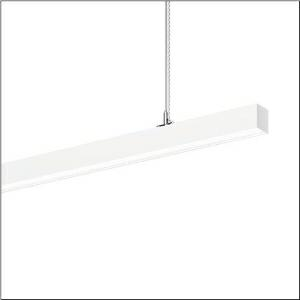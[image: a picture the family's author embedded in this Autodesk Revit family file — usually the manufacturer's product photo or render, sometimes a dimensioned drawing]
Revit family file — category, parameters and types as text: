
# Revit family: silica_r__21_51mx33da47wb_07b3
name_source: partatom
category: Lighting Fixtures
units: mm (PartAtom-declared; Revit-internal decimal feet)

## family parameters
Cut with Voids When Loaded = No
Host = Face
Light Source = No
Part Type = Normal
Room Calculation Point = No
Round Connector Dimension = Use Diameter
Shared = No

## types (1)
- --- (1 x LED, 5910 lm, 38.4 W, 4000K)
    Apparent Load = 38 VA
    CIE Flux Codes = 78 96 99 55 100
    Color Rendering = 80
    Color Temperature = 4000K
    Default Elevation = 1800 mm
    Description = Silica® 21, office luminaire, primary optical cover: prismatic diffuser, of PMMA, CAT 2 (L<= 3000cd/m²), light emission: direct/indirect distribution, primary light characteristic: symmetric, installation type: suspended mounting, LED, rated luminous flux: 5.910lm, luminous efficacy: 154lm/W, light colour: 840, colour temperature: 4000K, control gear: DALI 2, with terminal, 3+2-pole, max. 2.5mm², mains connection: 220..240V, AC, 50/60Hz, rated input power: 38.4W, luminaire housing, of aluminium, traffic white (RAL 9016), length: 1.204mm, width: 53mm, height: 53mm, protection rating (complete): IP20, insulation class (complete): insulation class I (protective earthing), certification: CE, permissible operating ambient temperature: 0..+35°C, standard: EN 50419, packaging unit: 1 piece
    Height = 53 mm
    Lamp = 1 x LED
    Lamp Light Flux = 5910 lm
    Lamp Power = 38.4 W
    Lamp count = 1
    Length = 1204 mm
    Luminous efficacy = 154 lm/W
    Manufacturer = Siteco
    ModVariant = No
    Model = 51MX33DA47WB
    Mounting Place = Ceiling
    Mounting Type = Pendant
    Number of Poles = 1
    OnlyDefault = Yes
    Power Factor = 1
    Product Name = Silica® 21
    Product group = office luminaire | ceiling pendant
    ProductGroupID = 904
    Protection Class = Protection class I
    Protection Degree = IP 20
    RLX_Detail_Level = 1
    RLX_Emergency_Light_Flux = 0 lm
    RLX_Emergency_Type = 0
    RLX_Emergency_Type_DB = No
    RlxData = <blob elided: 21217 chars, md5=289993e4>
    Socket = socket
    Standby Power = 0 W
    System Light Flux = 5910 lm
    System Power = 38 W
    Type Comments = factory setting: luminous flux: 100 % | dim-lin: 254 | 322 mA
    Type Image = l_1349007.jpg
    URL = http://relux.com
    VarID = @adj_118920
    Voltage = 0 V
    Weight = 0.00 kg
    Width = 53 mm

## geometry (parser evidence)
native form markers: Blend x4, Sweep x12
no freeform markers — native parametric forms only
